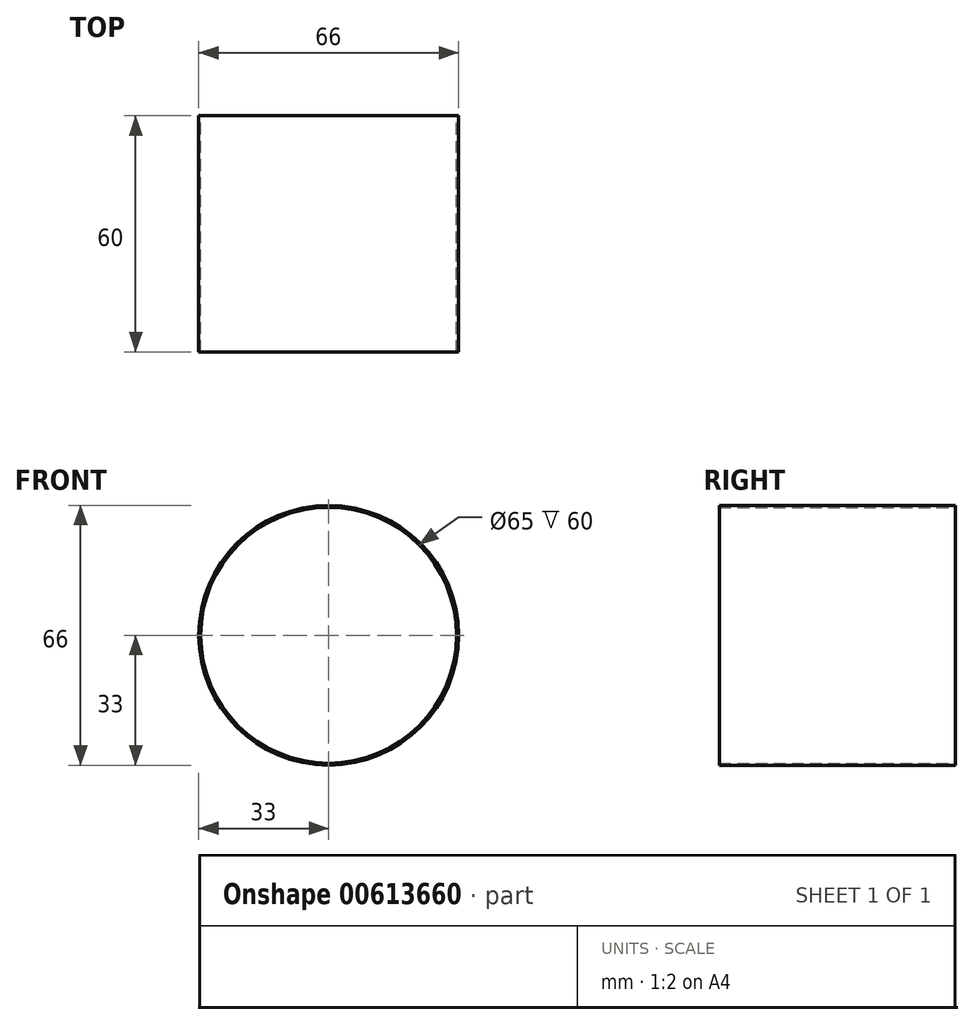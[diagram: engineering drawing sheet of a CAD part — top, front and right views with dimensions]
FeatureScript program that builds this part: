
annotation { "Feature Type Name" : "Feature", "Feature Type Description" : "" }
export const myFeature = defineFeature(function(context is Context, id is Id, definition is map)
    precondition{}
    {
        {
            var Q0;
            Q0=qCreatedBy(makeId("Front.planeOp"),FACE);
            var sketch = newSketch(context, id + "F0", { "sketchPlane" : qUnion([Q0])});
            skCircle(sketch, "E0", {"center": v(0, 0) * mm, "radius": 33 * mm});
            skCircle(sketch, "E1", {"center": v(0, 0) * mm, "radius": 32.5 * mm});
            skSolve(sketch);
        }
        {
            var Q0;
            Q0=makeQuery(id+"F0.imprint","IMPRINT",FACE,{"disambiguationData":[TD([[makeQuery(id+"F0.imprint","IMPRINT",EDGE,{"derivedFrom":sQuery(id+"F0.wireOp",EDGE,"E0")}),1.0]])]});
            extrude(context, id + "F1", {"entities" : qUnion([Q0]), "depth" : 60 * mm, "offsetDistance" : 25 * mm});
        }
    });
